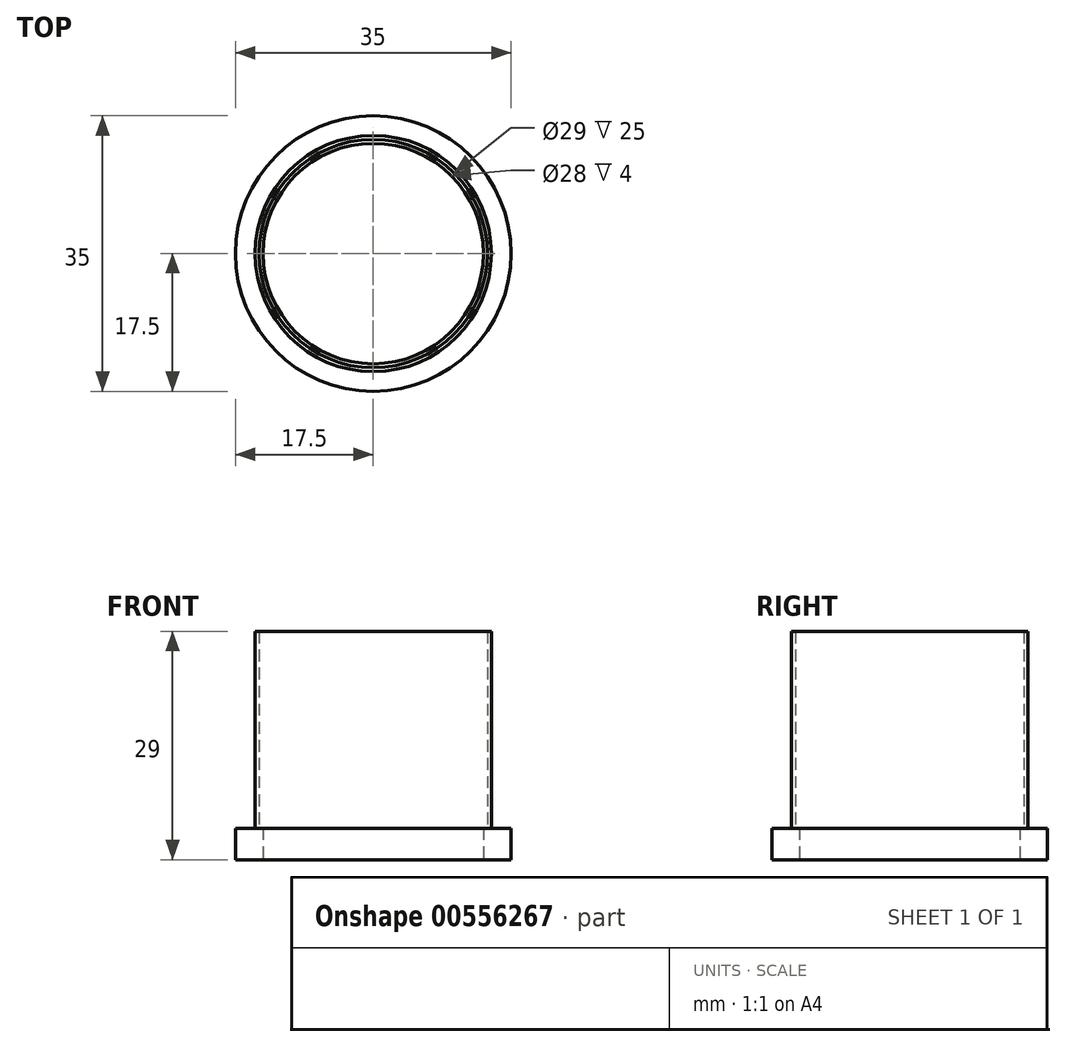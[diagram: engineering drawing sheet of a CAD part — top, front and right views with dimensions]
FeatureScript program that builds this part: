
annotation { "Feature Type Name" : "Feature", "Feature Type Description" : "" }
export const myFeature = defineFeature(function(context is Context, id is Id, definition is map)
    precondition{}
    {
        {
            var Q0;
            Q0=qCreatedBy(makeId("Top.planeOp"),FACE);
            var sketch = newSketch(context, id + "F0", { "sketchPlane" : qUnion([Q0])});
            skCircle(sketch, "E0", {"center": v(0, 0) * mm, "radius": 14 * mm});
            skCircle(sketch, "E1", {"center": v(0, 0) * mm, "radius": 17.5 * mm});
            skSolve(sketch);
        }
        {
            var Q0;
            Q0=makeQuery(id+"F0.imprint","IMPRINT",FACE,{"disambiguationData":[TD([[makeQuery(id+"F0.imprint","IMPRINT",EDGE,{"derivedFrom":sQuery(id+"F0.wireOp",EDGE,"E0")}),-1.0]])]});
            var Q1;
            Q1=sQuery(id+"F0.wireOp",EDGE,"E0");
            var Q2;
            Q2=sQuery(id+"F0.wireOp",EDGE,"E1");
            extrude(context, id + "F1", {"entities" : qUnion([Q0]), "surfaceEntities" : qUnion([Q1, Q2]), "depth" : 4 * mm, "offsetDistance" : 25 * mm});
        }
        {
            var Q0;
            Q0=makeQuery(id+"F1.opExtrude","CAP_FACE",FACE,{"disambiguationData":[OSD([sQuery(id+"F0.wireOp",EDGE,"E0"),sQuery(id+"F0.wireOp",EDGE,"E1")])],"isStart":false});
            var sketch = newSketch(context, id + "F2", { "sketchPlane" : qUnion([Q0])});
            skCircle(sketch, "E2", {"center": v(0, 0) * mm, "radius": 14.5 * mm});
            skCircle(sketch, "E3", {"center": v(0, 0) * mm, "radius": 15 * mm});
            skSolve(sketch);
        }
        {
            var Q0;
            Q0=qSketchRegion(id+"F2",true);
            extrude(context, id + "F3", {"entities" : qUnion([Q0]), "depth" : 25 * mm, "offsetDistance" : 25 * mm});
        }
    });
